# Revit family: 3. TacoNegro_PNormal_ESP
name_source: partatom
category: Generic Models
revit_build: Autodesk Revit 2015 (Build: 20140322_1515(x64)
units: mm (PartAtom-declared; Revit-internal decimal feet)

## types (2) — shared parameters
Absorción = Baja absorción
Acabado = Natural
Adherencia del mortero = >1N/mm2
Alto = 200 mm  [stored 0.656168 ft]
Ancho = 50 mm  [stored 0.164042 ft]
Aspecto = Rústico
Certificaciones = BBA - Reino Unido, Avis Technique - Francia, DIBt - Alemania, SINTEF - Noruega
Color principal = Negro
Color secundario = Marrón/Gris
Densidad aparente = Entre 80 y 100kg/m2
Description = Pieza de piedra natural montada sobre una base de cemento y reforzada con una malla de fibra de vidrio .
Posee sistema de anclaje patentado, de acero inoxidable, que permite su instalación a más de 2 metros de altura
Detalles constructivos = Detalles de:
- Instalación con perfil metálico
- Instalación de Stonepanel
- Instalación en muro interior
- Instalación del elemento de seguridad (cinta perforada + tacos)
- Esquinas entrantes
- Esquinas salientes
- Esquinas salientes pre-fabricadas
- Esquinas salientes mediante serrado del panel
- Esquinas salientes sin continuidad de Stonepanel (caso de una fachada lateral)
- Bordes superiores
- Sobre parapeto
- Marco de vano
Durabilidad = Según el certificado BBA, el sistema tiene una vida de diseño superior a 30 años.
Ensayos realizados por Avis Technique = Resistencia mecánica del anclaje, Resistencia mecánica de la cinta de seguridad, Ensayo de durabilidad tras la acción del agua, Ensayo de durabilidad tras la acción del hielo, Ensayo sísmico
Ensayos realizados por BBA = Resistencia a daños por heladicidad, Resistencia a choque térmico, Adherencia entre piedra y mortero, Resistencia al arrancamiento del anclaje, Resistencia a impacto
Ensayos realizados por DIBt = Adherencia entre piedra y mortero, Adherencia entre piedra y mortero tras 50 ciclos de hielo-deshielo
Ensayos realizados por SINTEF = Ensayo a los materiales de piedra, Ensayos a los paneles, Durabilidad y absorción de agua
Envejecimiento opr cambio térmicos = Sin alteraciones despues de 20 ciclos.
Forma = Forma de "s"
Forma de suministro = Los paneles se presentan en parejas, en un embalaje plástico o en cajas de cartón de 3 o 4 piezas.
Formato = 600x200
Impacto = -
Largo = 600 mm
Limpieza = En general, los paneles no requieren mantenimiento y son auto- limpiantes, pero la eliminación de algunos tipos de marcas pueden requerir un tratamiento especializado.
En caso de suciedad anormal, la superficie puede limpiarse con una mezcla / detergente doméstico y agua caliente , aplicada con una almohadilla de limpieza adecuado o una esponja.
Manufacturer = Cupastone
Material = Pizarra tradicional, de tonalidades negras y azuladas con tendencia a la oxidación en exteriores, para crear paredes o fachadas únicas, elegantes y llenas de personalidad.
Model = Stonpanel® SKY Taco Negro
NBS Reference = 45-25-45/380 Natural stone panels
Número de serie = SPZ-19A
Omniclass = 23-15 15 15 11
Otros datos de interés del producto = Dispone de un anclaje para instalar a alturas superiores a 2 metros
Oxidación = No oxida
Peso = 9 kg
Resistencia = Buena resistencia
Resistencia a la flexión = -
Resistencia al fuego = No combustible
Resistencia al hielo = Sin alteraciones despues de 50 ciclos
Sistema de anclaje = Cinta perforada en acero inoxidable:
- Naturaleza del acero: AISI 316 (1.4401) o AISI 304 (1.4301)
- Espesor mínimo (mm) : 0,7
- Ancho (mm) : 12 a 15
- Diámetro del hueco (mm) : 6 ± 1

Tacos:
La elección de los tacos y clavijas de fijación debe ser realizada teniendo en cuenta la acción en depresión del viento (muros exteriores) y de la resistencia de los tacos en el soporte, en función de la naturaleza del soporte.
Type Image = <None>
URL = http://www.cupastone.es
Uniclass 2 = Pr_25_71_14_56 Natural stone panels
Uniclass 2015 = Pr_25_71_14_56 Natural stone panels
Usos Indicados = Revestimiento de Paredes exteriores e interiores en edificaciones nuevas o rehabilitaciones
Ventajas de Stonepanel = Eficaz: Instalación ágil y sencilla : 10 veces más rápido que la mampostería tradicional (Ritmo medio de colocación de 20 m2/día). Mayor rentabilidad gracias al menor desperdicio de material en obra y a la durabilidad de un producto natural frente a otros revestimientos. La colocación de los paneles no requiere mano de obra ni maquinaria especializada.
Seguro: Un sistema de anclaje patentado, de acero inoxidable, que permite su instalación a más de 2 metros de altura. Base de cemento homogénea y rugosa que garantiza la adhesión y permite el corte sin desprendimiento.
Calidad: Control permanente del proceso de producción desde la oficina I+D+I. Una cuidada selección de piedra natural realizada por los expertos de CUPASTONE. Disponibilidad de piezas especiales para adaptarse perfectamente a cada edificio: esquinas (macizas, rectas, dobles o para ventanas), cubremuros, y otros complementarios.
Estética: Forma de “S” que evita la visión de las juntas para homogenizar el aspecto final. Gran variedad de paneles para elegir entre colores y acabados de piedra natural. La propia belleza y exclusividad de la piedra natural: Cada piedra es
única.
zero-valued in all types: Desfase de altura

## type names (no varying parameters)
- Stonepanel® SKY Taco Negro
- Stonepanel® SKY Taco Negro. 20 cm - 60 cm

note: [stored X ft] marks values corroborated as IEEE doubles in the binary element streams (Revit-internal decimal feet)
